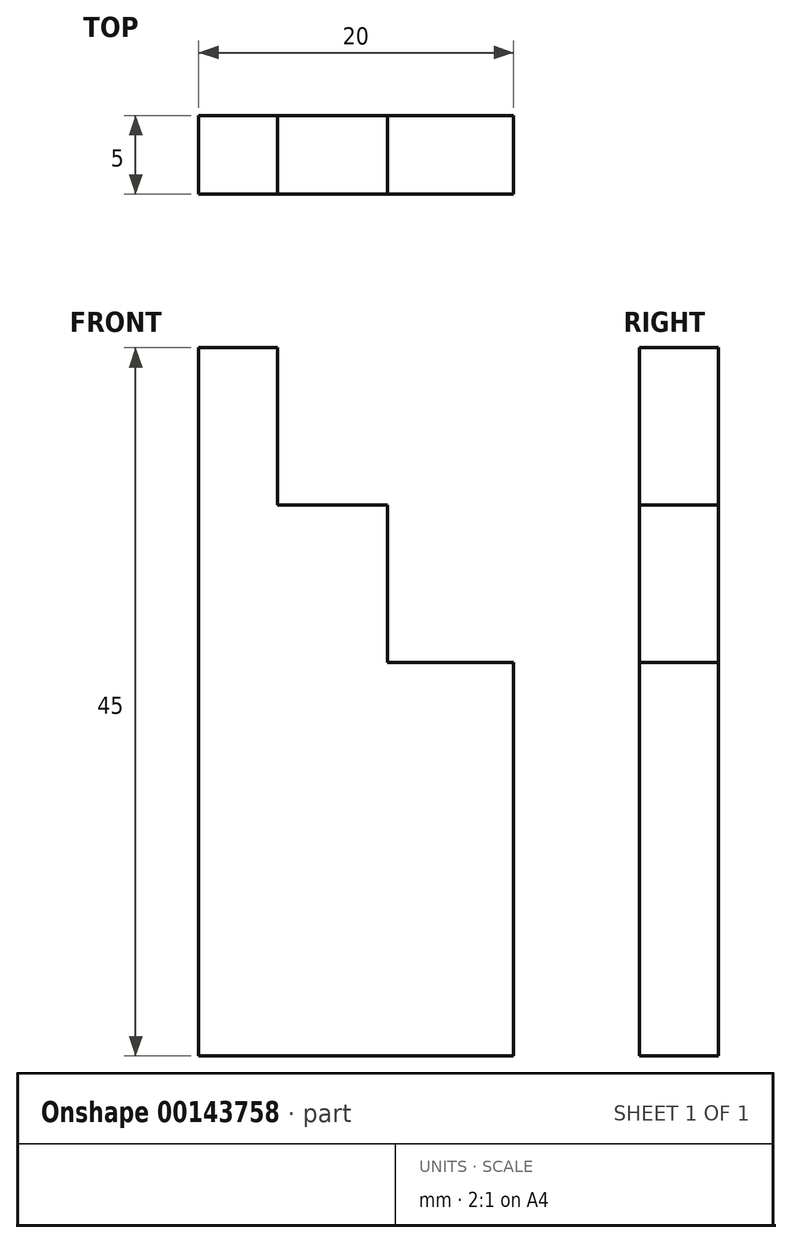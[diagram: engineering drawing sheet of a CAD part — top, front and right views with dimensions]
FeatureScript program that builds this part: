
annotation { "Feature Type Name" : "Feature", "Feature Type Description" : "" }
export const myFeature = defineFeature(function(context is Context, id is Id, definition is map)
    precondition{}
    {
        {
            var Q0;
            Q0=qCreatedBy(makeId("Front.planeOp"),FACE);
            var sketch = newSketch(context, id + "F0", { "sketchPlane" : qUnion([Q0])});
            skLineSegment(sketch, "E0", {"start": v(0, 0) * mm, "end": v(0, 45) * mm});
            skLineSegment(sketch, "E1", {"start": v(0, 45) * mm, "end": v(5, 45) * mm});
            skLineSegment(sketch, "E2", {"start": v(5, 45) * mm, "end": v(5, 35) * mm});
            skLineSegment(sketch, "E3", {"start": v(5, 35) * mm, "end": v(12, 35) * mm});
            skLineSegment(sketch, "E4", {"start": v(12, 35) * mm, "end": v(12, 25) * mm});
            skLineSegment(sketch, "E5", {"start": v(12, 25) * mm, "end": v(20, 25) * mm});
            skLineSegment(sketch, "E6", {"start": v(20, 25) * mm, "end": v(20, 0) * mm});
            skLineSegment(sketch, "E7", {"start": v(20, 0) * mm, "end": v(0, 0) * mm});
            skSolve(sketch);
        }
        {
            var Q0;
            Q0=qSketchRegion(id+"F0",true);
            extrude(context, id + "F1", {"entities" : qUnion([Q0]), "depth" : 5 * mm});
        }
    });
